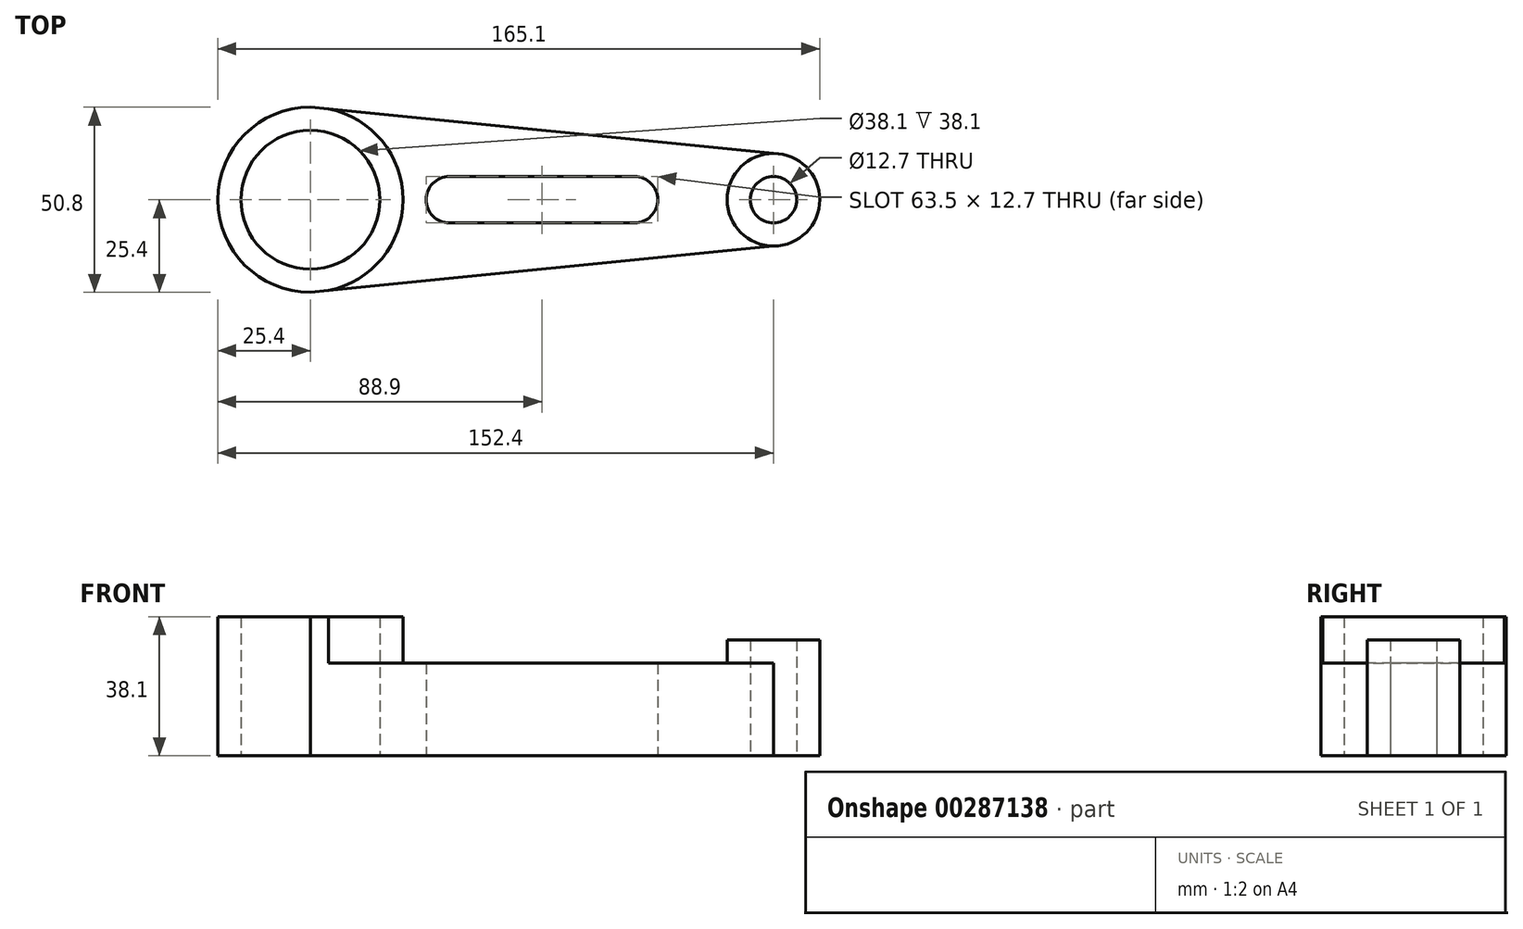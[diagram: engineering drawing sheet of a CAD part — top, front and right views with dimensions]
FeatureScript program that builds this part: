
annotation { "Feature Type Name" : "Feature", "Feature Type Description" : "" }
export const myFeature = defineFeature(function(context is Context, id is Id, definition is map)
    precondition{}
    {
        {
            var Q0;
            Q0=qCreatedBy(makeId("Top.planeOp"),FACE);
            var sketch = newSketch(context, id + "F0", { "sketchPlane" : qUnion([Q0])});
            skArc(sketch, "E0", {"start": v(-25.4, 6.35) * mm, "mid": v(-31.75, 0) * mm, "end": v(-25.4, -6.35) * mm});
            skArc(sketch, "E1", {"start": v(25.4, -6.35) * mm, "mid": v(31.75, 0) * mm, "end": v(25.4, 6.35) * mm});
            skCircle(sketch, "E2", {"center": v(-63.5, 0) * mm, "radius": 19.05 * mm});
            skCircle(sketch, "E3", {"center": v(-63.5, 0) * mm, "radius": 25.4 * mm});
            skCircle(sketch, "E4", {"center": v(63.5, 0) * mm, "radius": 6.35 * mm});
            skCircle(sketch, "E5", {"center": v(63.5, 0) * mm, "radius": 12.7 * mm});
            skLineSegment(sketch, "E6", {"start": v(-25.4, 6.35) * mm, "end": v(25.4, 6.35) * mm});
            skLineSegment(sketch, "E7", {"start": v(25.4, -6.35) * mm, "end": v(-25.4, -6.35) * mm});
            skLineSegment(sketch, "E8", {"start": v(63.5, -12.7) * mm, "end": v(-63.5, -25.4) * mm});
            skLineSegment(sketch, "E9", {"start": v(-63.5, 25.4) * mm, "end": v(63.5, 12.7) * mm});
            skSolve(sketch);
        }
        {
            var Q0;
            Q0=makeQuery(id+"F0.imprint","IMPRINT",FACE,{"disambiguationData":[TD([[makeQuery(id+"F0.imprint","IMPRINT",EDGE,{"derivedFrom":sQuery(id+"F0.wireOp",EDGE,"E2")}),-1.0]])]});
            extrude(context, id + "F1", {"entities" : qUnion([Q0]), "depth" : 38.1 * mm});
        }
        {
            var Q0;
            Q0=makeQuery(id+"F0.imprint","IMPRINT",FACE,{"disambiguationData":[TD([[makeQuery(id+"F0.imprint","IMPRINT",EDGE,{"derivedFrom":sQuery(id+"F0.wireOp",EDGE,"E0")}),-1.0]])]});
            extrude(context, id + "F2", {"entities" : qUnion([Q0]), "operationType" : NewBodyOperationType.ADD, "depth" : 25.4 * mm});
        }
        {
            var Q0;
            Q0=makeQuery(id+"F0.imprint","IMPRINT",FACE,{"disambiguationData":[TD([[makeQuery(id+"F0.imprint","IMPRINT",EDGE,{"derivedFrom":sQuery(id+"F0.wireOp",EDGE,"E4")}),-1.0]])]});
            extrude(context, id + "F3", {"entities" : qUnion([Q0]), "operationType" : NewBodyOperationType.ADD, "depth" : 31.75 * mm});
        }
    });
